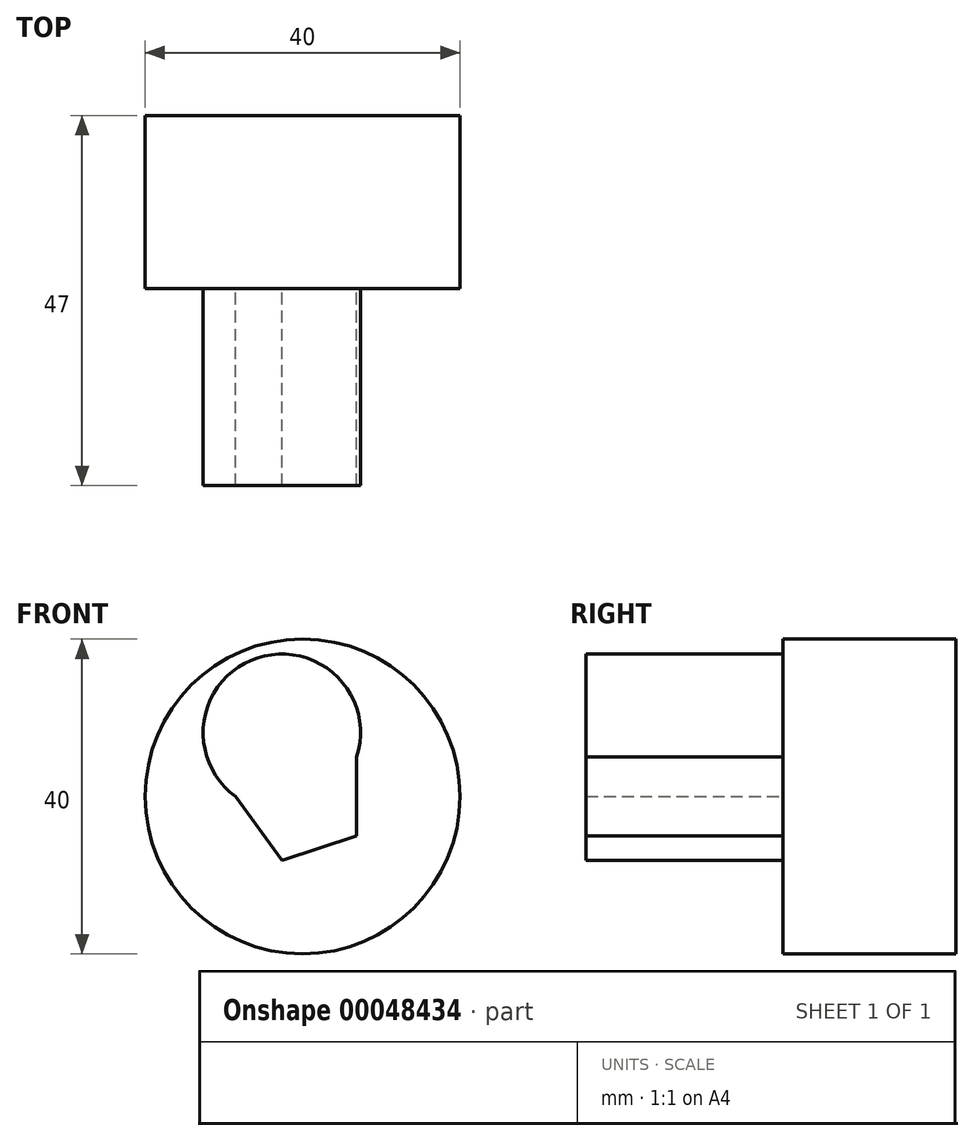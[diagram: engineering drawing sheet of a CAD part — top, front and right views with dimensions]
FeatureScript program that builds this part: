
annotation { "Feature Type Name" : "Feature", "Feature Type Description" : "" }
export const myFeature = defineFeature(function(context is Context, id is Id, definition is map)
    precondition{}
    {
        {
            var Q0;
            Q0=qCreatedBy(makeId("Front.planeOp"),FACE);
            var sketch = newSketch(context, id + "F0", { "sketchPlane" : qUnion([Q0])});
            skCircle(sketch, "E0", {"center": v(0, 0) * mm, "radius": 20 * mm});
            skSolve(sketch);
        }
        {
            var Q0;
            Q0=makeQuery(id+"F0.imprint","IMPRINT",FACE,{"disambiguationData":[TD([[makeQuery(id+"F0.imprint","IMPRINT",EDGE,{"derivedFrom":sQuery(id+"F0.wireOp",EDGE,"E0")}),1.0]])]});
            extrude(context, id + "F1", {"entities" : qUnion([Q0]), "depth" : 22 * mm});
        }
        {
            var Q0;
            Q0=makeQuery(id+"F1.opExtrude","CAP_FACE",FACE,{"disambiguationData":[OSD([sQuery(id+"F0.wireOp",EDGE,"E0")])],"isStart":false});
            var sketch = newSketch(context, id + "F2", { "sketchPlane" : qUnion([Q0])});
            skCircle(sketch, "E1.cCircle", {"center": v(0, 0) * mm, "radius": 6.88 * mm, "construction": true});
            skLineSegment(sketch, "E1.0", {"start": v(6.88, 5) * mm, "end": v(6.88, -5) * mm});
            skLineSegment(sketch, "E1.1", {"start": v(6.88, -5) * mm, "end": v(-2.63, -8.1) * mm});
            skLineSegment(sketch, "E1.2", {"start": v(-2.63, -8.1) * mm, "end": v(-8.5, 0) * mm});
            skLineSegment(sketch, "E1.3", {"start": v(-8.5, 0) * mm, "end": v(-2.63, 8.1) * mm});
            skLineSegment(sketch, "E1.4", {"start": v(-2.63, 8.1) * mm, "end": v(6.88, 5) * mm});
            skPoint(sketch, "E1.0.midPoint", {"position": v(6.88, 0) * mm});
            skSolve(sketch);
        }
        {
            var Q0;
            Q0=makeQuery(id+"F2.imprint","IMPRINT",FACE,{"disambiguationData":[TD([[makeQuery(id+"F2.imprint","IMPRINT",EDGE,{"derivedFrom":sQuery(id+"F2.wireOp",EDGE,"E1.0")}),-1.0]])]});
            extrude(context, id + "F3", {"entities" : qUnion([Q0]), "operationType" : NewBodyOperationType.ADD, "depth" : 25 * mm});
        }
        {
            var Q0;
            Q0=makeQuery(id+"F3.opExtrude","SWEPT_FACE",FACE,{"disambiguationData":[OSD([sQuery(id+"F2.wireOp",EDGE,"E1.4")])]});
            var sketch = newSketch(context, id + "F4", { "sketchPlane" : qUnion([Q0])});
            skLineSegment(sketch, "E2.0.0", {"start": v(5, -22) * mm, "end": v(-5, -22) * mm});
            skLineSegment(sketch, "E2.0.1", {"start": v(-5, -22) * mm, "end": v(-5, -47) * mm});
            skLineSegment(sketch, "E2.0.2", {"start": v(-5, -47) * mm, "end": v(5, -47) * mm});
            skLineSegment(sketch, "E2.0.3", {"start": v(5, -47) * mm, "end": v(5, -22) * mm});
            skSolve(sketch);
        }
        {
            var Q0;
            Q0=makeQuery(id+"F4.imprint","IMPRINT",FACE,{"disambiguationData":[TD([[makeQuery(id+"F4.imprint","IMPRINT",EDGE,{"derivedFrom":sQuery(id+"F4.wireOp",EDGE,"E2.0.0")}),-1.0]])]});
            var Q1;
            Q1=sQuery(id+"F4.wireOp",EDGE,"E2.0.1");
            revolve(context, id + "F5", {"operationType" : NewBodyOperationType.ADD, "entities" : qUnion([Q0]), "axis" : qUnion([Q1]), "revolveType" : RevolveType.FULL});
        }
    });
